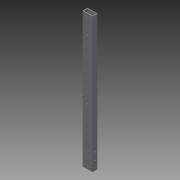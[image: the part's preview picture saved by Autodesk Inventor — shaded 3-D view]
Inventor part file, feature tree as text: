
AUTODESK INVENTOR PART (.ipt)
format: ipt  version: 2013 (Build 170138000, 138)  size: 148,992 bytes
history: native  units: in
note: dims shown in document units (in); Inventor stores cm internally (conversion verified against a paired STEP export)
features: sketch x7, extrude x6, hole x1
ambient origin geometry x8: Origin, YZ Plane, XZ Plane, XY Plane, X Axis, Y Axis, Z Axis, Center Point
bodies: Solid1 (feature_tree)
feature tree (14):
  extrude  "Extrusion1"  Depth=1.0in
  extrude  "Extrusion2"  Depth=0.75in
  extrude  "Extrusion4"  Depth=1.0in
  extrude  "Extrusion6"  Depth=0.5in
  extrude  "Extrusion9"  Depth=0.5in TaperAngle=0.0deg
  hole  "Hole1"  [1 undecoded]
  extrude  "Extrusion10"  Depth=2.0in
  sketch  "Sketch1"  dims[d0=2.0in d1=1.0in]
  sketch  "Sketch2"  dims[d2=1.75in d3=0.75in]
  sketch  "Sketch4"  dims[d4=24.0in d5=0.0in d6=1.0in]
  sketch  "Sketch6"  dims[d7=1.0in d8=0.5in]
  sketch  "Sketch8"  dims[d9=24.0in d10=0.0in d25=0.5in d26=0.0in]
  sketch  "Sketch9"  dims[d35=2.5in d36=0.0in d49=13.543in]
  sketch  "Sketch10"  dims[d50=90.0deg d51=2.0in d52=180.0deg d53=0.25in d54=0.25in d55=2.0in d56=0.0in d57=3.313in d58=1.5in d59=90.0deg d60=0.25in d61=0.75in d62=0.375in d63=0.25in d64=0.5635in d65=1.0in d66=0.8108in d67=17.0in d68=2.0in d69=180.0deg d70=0.25in d71=0.25in d72=2.0in d73=0.0in]
note: 1 required parameter value undecoded (feature->parameter linkage not recoverable at this tier; creation-order binding heuristic only, values carry confidence <= 0.55)
